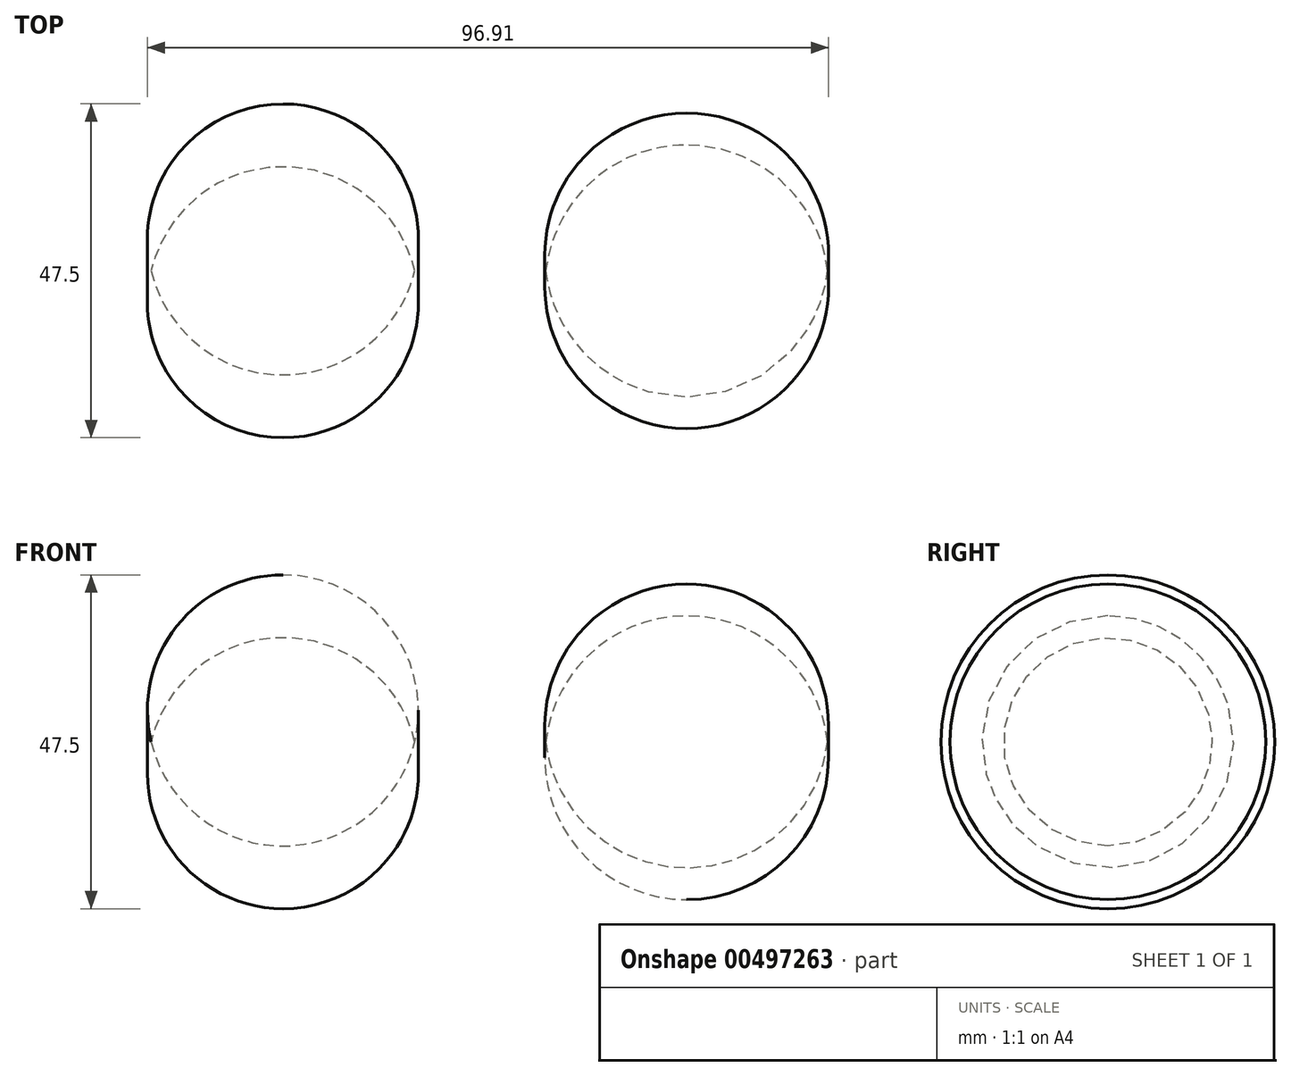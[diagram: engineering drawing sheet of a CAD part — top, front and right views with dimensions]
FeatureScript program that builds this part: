
annotation { "Feature Type Name" : "Feature", "Feature Type Description" : "" }
export const myFeature = defineFeature(function(context is Context, id is Id, definition is map)
    precondition{}
    {
        {
            var Q0;
            Q0=qCreatedBy(makeId("Top.planeOp"),FACE);
            var sketch = newSketch(context, id + "F0", { "sketchPlane" : qUnion([Q0])});
            skArc(sketch, "E0", {"start": v(-37.52, 0) * mm, "mid": v(-18.76, -23.75) * mm, "end": v(0, 0) * mm});
            skLineSegment(sketch, "E1", {"start": v(-37.52, 0) * mm, "end": v(0, 0) * mm});
            skSolve(sketch);
        }
        {
            var Q0;
            Q0=makeQuery(id+"F0.imprint","IMPRINT",FACE,{"disambiguationData":[TD([[makeQuery(id+"F0.imprint","IMPRINT",EDGE,{"derivedFrom":sQuery(id+"F0.wireOp",EDGE,"E0")}),1.0]])]});
            var Q1;
            Q1=sQuery(id+"F0.wireOp",EDGE,"E1");
            revolve(context, id + "F1", {"entities" : qUnion([Q0]), "axis" : qUnion([Q1]), "revolveType" : RevolveType.FULL});
        }
        {
            var Q0;
            Q0=qCreatedBy(makeId("Top.planeOp"),FACE);
            var sketch = newSketch(context, id + "F2", { "sketchPlane" : qUnion([Q0])});
            skArc(sketch, "E2", {"start": v(58.74, 0) * mm, "mid": v(38.68, 22.45) * mm, "end": v(18.62, 0) * mm});
            skLineSegment(sketch, "E3", {"start": v(58.74, 0) * mm, "end": v(18.62, 0) * mm});
            skSolve(sketch);
        }
        {
            var Q0;
            Q0=makeQuery(id+"F2.imprint","IMPRINT",FACE,{"disambiguationData":[TD([[makeQuery(id+"F2.imprint","IMPRINT",EDGE,{"derivedFrom":sQuery(id+"F2.wireOp",EDGE,"E2")}),1.0]])]});
            var Q1;
            Q1=sQuery(id+"F2.wireOp",EDGE,"E3");
            revolve(context, id + "F3", {"entities" : qUnion([Q0]), "axis" : qUnion([Q1]), "revolveType" : RevolveType.FULL});
        }
    });
